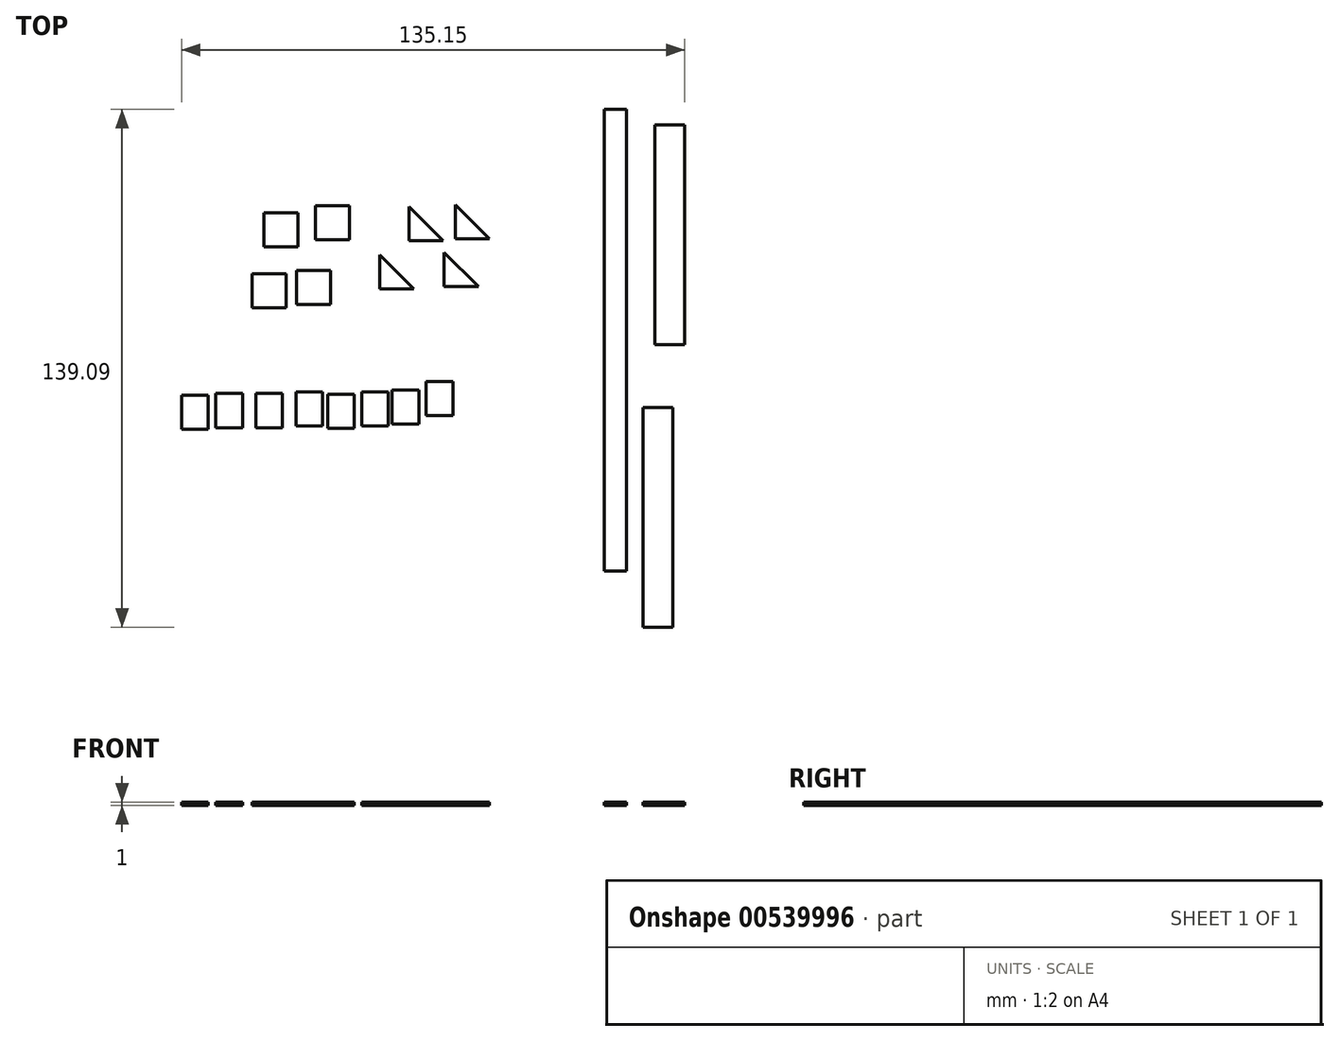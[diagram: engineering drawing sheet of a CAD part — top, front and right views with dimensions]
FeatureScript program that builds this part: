
annotation { "Feature Type Name" : "Feature", "Feature Type Description" : "" }
export const myFeature = defineFeature(function(context is Context, id is Id, definition is map)
    precondition{}
    {
        {
            var Q0;
            Q0=qCreatedBy(makeId("Top.planeOp"),FACE);
            var sketch = newSketch(context, id + "F0", { "sketchPlane" : qUnion([Q0])});
            skLineSegment(sketch, "E0.bottom", {"start": v(-71.16, 32.3) * mm, "end": v(-80.3, 32.3) * mm});
            skLineSegment(sketch, "E0.top", {"start": v(-71.16, 41.45) * mm, "end": v(-80.3, 41.45) * mm});
            skLineSegment(sketch, "E0.left", {"start": v(-71.16, 32.3) * mm, "end": v(-71.16, 41.45) * mm});
            skLineSegment(sketch, "E0.right", {"start": v(-80.3, 32.3) * mm, "end": v(-80.3, 41.45) * mm});
            skPoint(sketch, "E0.middle", {"position": v(-75.73, 36.88) * mm});
            skLineSegment(sketch, "E1.bottom", {"start": v(-74.39, 15.94) * mm, "end": v(-83.54, 15.94) * mm});
            skLineSegment(sketch, "E1.top", {"start": v(-74.39, 25.09) * mm, "end": v(-83.54, 25.09) * mm});
            skLineSegment(sketch, "E1.left", {"start": v(-74.39, 15.94) * mm, "end": v(-74.39, 25.09) * mm});
            skLineSegment(sketch, "E1.right", {"start": v(-83.54, 15.94) * mm, "end": v(-83.54, 25.09) * mm});
            skPoint(sketch, "E1.middle", {"position": v(-78.96, 20.51) * mm});
            skLineSegment(sketch, "E2.bottom", {"start": v(-57.33, 34.15) * mm, "end": v(-66.48, 34.15) * mm});
            skLineSegment(sketch, "E2.top", {"start": v(-57.33, 43.3) * mm, "end": v(-66.48, 43.3) * mm});
            skLineSegment(sketch, "E2.left", {"start": v(-57.33, 34.15) * mm, "end": v(-57.33, 43.3) * mm});
            skLineSegment(sketch, "E2.right", {"start": v(-66.48, 34.15) * mm, "end": v(-66.48, 43.3) * mm});
            skPoint(sketch, "E2.middle", {"position": v(-61.9, 38.72) * mm});
            skLineSegment(sketch, "E3.bottom", {"start": v(-62.4, 16.74) * mm, "end": v(-71.55, 16.74) * mm});
            skLineSegment(sketch, "E3.top", {"start": v(-62.4, 25.9) * mm, "end": v(-71.55, 25.9) * mm});
            skLineSegment(sketch, "E3.left", {"start": v(-62.4, 16.74) * mm, "end": v(-62.4, 25.9) * mm});
            skLineSegment(sketch, "E3.right", {"start": v(-71.55, 16.74) * mm, "end": v(-71.55, 25.9) * mm});
            skPoint(sketch, "E3.middle", {"position": v(-66.97, 21.32) * mm});
            skLineSegment(sketch, "E4", {"start": v(-41.27, 43.03) * mm, "end": v(-41.27, 33.88) * mm});
            skLineSegment(sketch, "E5", {"start": v(-41.27, 33.88) * mm, "end": v(-32.12, 33.88) * mm});
            skLineSegment(sketch, "E6", {"start": v(-41.27, 43.03) * mm, "end": v(-32.12, 33.88) * mm});
            skLineSegment(sketch, "E7", {"start": v(-49.16, 30.07) * mm, "end": v(-49.16, 20.92) * mm});
            skLineSegment(sketch, "E8", {"start": v(-49.16, 20.92) * mm, "end": v(-40.01, 20.92) * mm});
            skLineSegment(sketch, "E9", {"start": v(-49.16, 30.07) * mm, "end": v(-40.01, 20.92) * mm});
            skLineSegment(sketch, "E10", {"start": v(-31.87, 30.76) * mm, "end": v(-31.87, 21.61) * mm});
            skLineSegment(sketch, "E11", {"start": v(-31.87, 21.61) * mm, "end": v(-22.72, 21.61) * mm});
            skLineSegment(sketch, "E12", {"start": v(-31.87, 30.76) * mm, "end": v(-22.72, 21.61) * mm});
            skLineSegment(sketch, "E13", {"start": v(-28.87, 43.56) * mm, "end": v(-28.87, 34.4) * mm});
            skLineSegment(sketch, "E14", {"start": v(-28.87, 34.4) * mm, "end": v(-19.72, 34.4) * mm});
            skLineSegment(sketch, "E15", {"start": v(-28.87, 43.56) * mm, "end": v(-19.72, 34.4) * mm});
            skSolve(sketch);
        }
        {
            var Q0;
            Q0=makeQuery(id+"F0.imprint","IMPRINT",FACE,{"disambiguationData":[TD([[makeQuery(id+"F0.imprint","IMPRINT",EDGE,{"derivedFrom":sQuery(id+"F0.wireOp",EDGE,"E0.bottom")}),-1.0]])]});
            var Q1;
            Q1=makeQuery(id+"F0.imprint","IMPRINT",FACE,{"disambiguationData":[TD([[makeQuery(id+"F0.imprint","IMPRINT",EDGE,{"derivedFrom":sQuery(id+"F0.wireOp",EDGE,"E1.bottom")}),-1.0]])]});
            var Q2;
            Q2=makeQuery(id+"F0.imprint","IMPRINT",FACE,{"disambiguationData":[TD([[makeQuery(id+"F0.imprint","IMPRINT",EDGE,{"derivedFrom":sQuery(id+"F0.wireOp",EDGE,"E2.bottom")}),-1.0]])]});
            var Q3;
            Q3=makeQuery(id+"F0.imprint","IMPRINT",FACE,{"disambiguationData":[TD([[makeQuery(id+"F0.imprint","IMPRINT",EDGE,{"derivedFrom":sQuery(id+"F0.wireOp",EDGE,"E3.bottom")}),-1.0]])]});
            var Q4;
            Q4=makeQuery(id+"F0.imprint","IMPRINT",FACE,{"disambiguationData":[TD([[makeQuery(id+"F0.imprint","IMPRINT",EDGE,{"derivedFrom":sQuery(id+"F0.wireOp",EDGE,"E7")}),1.0]])]});
            var Q5;
            Q5=makeQuery(id+"F0.imprint","IMPRINT",FACE,{"disambiguationData":[TD([[makeQuery(id+"F0.imprint","IMPRINT",EDGE,{"derivedFrom":sQuery(id+"F0.wireOp",EDGE,"E10")}),1.0]])]});
            var Q6;
            Q6=makeQuery(id+"F0.imprint","IMPRINT",FACE,{"disambiguationData":[TD([[makeQuery(id+"F0.imprint","IMPRINT",EDGE,{"derivedFrom":sQuery(id+"F0.wireOp",EDGE,"E4")}),1.0]])]});
            var Q7;
            Q7=makeQuery(id+"F0.imprint","IMPRINT",FACE,{"disambiguationData":[TD([[makeQuery(id+"F0.imprint","IMPRINT",EDGE,{"derivedFrom":sQuery(id+"F0.wireOp",EDGE,"E13")}),1.0]])]});
            extrude(context, id + "F1", {"entities" : qUnion([Q0, Q1, Q2, Q3, Q4, Q5, Q6, Q7]), "depth" : 1 * mm, "offsetDistance" : 25 * mm});
        }
        {
            var Q0;
            Q0=qCreatedBy(makeId("Top.planeOp"),FACE);
            var sketch = newSketch(context, id + "F2", { "sketchPlane" : qUnion([Q0])});
            skLineSegment(sketch, "E16.bottom", {"start": v(-95.29, -16.75) * mm, "end": v(-102.44, -16.75) * mm});
            skLineSegment(sketch, "E16.top", {"start": v(-95.29, -7.6) * mm, "end": v(-102.44, -7.6) * mm});
            skLineSegment(sketch, "E16.left", {"start": v(-95.29, -16.75) * mm, "end": v(-95.29, -7.6) * mm});
            skLineSegment(sketch, "E16.right", {"start": v(-102.44, -16.75) * mm, "end": v(-102.44, -7.6) * mm});
            skPoint(sketch, "E16.middle", {"position": v(-98.86, -12.18) * mm});
            skLineSegment(sketch, "E17.bottom", {"start": v(-86.08, -16.3) * mm, "end": v(-93.23, -16.3) * mm});
            skLineSegment(sketch, "E17.top", {"start": v(-86.08, -7.15) * mm, "end": v(-93.23, -7.15) * mm});
            skLineSegment(sketch, "E17.left", {"start": v(-86.08, -16.3) * mm, "end": v(-86.08, -7.15) * mm});
            skLineSegment(sketch, "E17.right", {"start": v(-93.23, -16.3) * mm, "end": v(-93.23, -7.15) * mm});
            skPoint(sketch, "E17.middle", {"position": v(-89.65, -11.73) * mm});
            skLineSegment(sketch, "E18.bottom", {"start": v(-75.3, -16.3) * mm, "end": v(-82.45, -16.3) * mm});
            skLineSegment(sketch, "E18.top", {"start": v(-75.3, -7.15) * mm, "end": v(-82.45, -7.15) * mm});
            skLineSegment(sketch, "E18.left", {"start": v(-75.3, -16.3) * mm, "end": v(-75.3, -7.15) * mm});
            skLineSegment(sketch, "E18.right", {"start": v(-82.45, -16.3) * mm, "end": v(-82.45, -7.15) * mm});
            skPoint(sketch, "E18.middle", {"position": v(-78.87, -11.73) * mm});
            skLineSegment(sketch, "E19.bottom", {"start": v(-64.52, -15.81) * mm, "end": v(-71.67, -15.81) * mm});
            skLineSegment(sketch, "E19.top", {"start": v(-64.52, -6.66) * mm, "end": v(-71.67, -6.66) * mm});
            skLineSegment(sketch, "E19.left", {"start": v(-64.52, -15.81) * mm, "end": v(-64.52, -6.66) * mm});
            skLineSegment(sketch, "E19.right", {"start": v(-71.67, -15.81) * mm, "end": v(-71.67, -6.66) * mm});
            skPoint(sketch, "E19.middle", {"position": v(-68.1, -11.24) * mm});
            skLineSegment(sketch, "E20.bottom", {"start": v(-56.02, -16.47) * mm, "end": v(-63.17, -16.47) * mm});
            skLineSegment(sketch, "E20.top", {"start": v(-56.02, -7.32) * mm, "end": v(-63.17, -7.32) * mm});
            skLineSegment(sketch, "E20.left", {"start": v(-56.02, -16.47) * mm, "end": v(-56.02, -7.32) * mm});
            skLineSegment(sketch, "E20.right", {"start": v(-63.17, -16.47) * mm, "end": v(-63.17, -7.32) * mm});
            skPoint(sketch, "E20.middle", {"position": v(-59.6, -11.9) * mm});
            skLineSegment(sketch, "E21.bottom", {"start": v(-46.88, -15.81) * mm, "end": v(-54.03, -15.81) * mm});
            skLineSegment(sketch, "E21.top", {"start": v(-46.88, -6.66) * mm, "end": v(-54.03, -6.66) * mm});
            skLineSegment(sketch, "E21.left", {"start": v(-46.88, -15.81) * mm, "end": v(-46.88, -6.66) * mm});
            skLineSegment(sketch, "E21.right", {"start": v(-54.03, -15.81) * mm, "end": v(-54.03, -6.66) * mm});
            skPoint(sketch, "E21.middle", {"position": v(-50.45, -11.24) * mm});
            skLineSegment(sketch, "E22.bottom", {"start": v(-38.71, -15.32) * mm, "end": v(-45.86, -15.32) * mm});
            skLineSegment(sketch, "E22.top", {"start": v(-38.71, -6.17) * mm, "end": v(-45.86, -6.17) * mm});
            skLineSegment(sketch, "E22.left", {"start": v(-38.71, -15.32) * mm, "end": v(-38.71, -6.17) * mm});
            skLineSegment(sketch, "E22.right", {"start": v(-45.86, -15.32) * mm, "end": v(-45.86, -6.17) * mm});
            skPoint(sketch, "E22.middle", {"position": v(-42.29, -10.75) * mm});
            skLineSegment(sketch, "E23.bottom", {"start": v(-29.57, -13.04) * mm, "end": v(-36.72, -13.04) * mm});
            skLineSegment(sketch, "E23.top", {"start": v(-29.57, -3.89) * mm, "end": v(-36.72, -3.89) * mm});
            skLineSegment(sketch, "E23.left", {"start": v(-29.57, -13.04) * mm, "end": v(-29.57, -3.89) * mm});
            skLineSegment(sketch, "E23.right", {"start": v(-36.72, -13.04) * mm, "end": v(-36.72, -3.89) * mm});
            skPoint(sketch, "E23.middle", {"position": v(-33.14, -8.46) * mm});
            skSolve(sketch);
        }
        {
            var Q0;
            Q0 = qSketchRegion(id + "F2", true);
            extrude(context, id + "F3", {"entities" : qUnion([Q0]), "depth" : 1 * mm, "offsetDistance" : 25 * mm});
        }
        {
            var Q0;
            Q0=qCreatedBy(makeId("Top.planeOp"),FACE);
            var sketch = newSketch(context, id + "F4", { "sketchPlane" : qUnion([Q0])});
            skLineSegment(sketch, "E24.bottom", {"start": v(11.14, 69.19) * mm, "end": v(17.14, 69.19) * mm});
            skLineSegment(sketch, "E24.top", {"start": v(11.14, -54.86) * mm, "end": v(17.14, -54.86) * mm});
            skLineSegment(sketch, "E24.left", {"start": v(11.14, 69.19) * mm, "end": v(11.14, -54.86) * mm});
            skLineSegment(sketch, "E24.right", {"start": v(17.14, 69.19) * mm, "end": v(17.14, -54.86) * mm});
            skLineSegment(sketch, "E25.bottom", {"start": v(24.69, 65.02) * mm, "end": v(32.71, 65.02) * mm});
            skLineSegment(sketch, "E25.top", {"start": v(24.69, 6) * mm, "end": v(32.71, 6) * mm});
            skLineSegment(sketch, "E25.left", {"start": v(24.69, 65.02) * mm, "end": v(24.69, 6) * mm});
            skLineSegment(sketch, "E25.right", {"start": v(32.71, 65.02) * mm, "end": v(32.71, 6) * mm});
            skLineSegment(sketch, "E26.bottom", {"start": v(21.54, -10.87) * mm, "end": v(29.56, -10.87) * mm});
            skLineSegment(sketch, "E26.top", {"start": v(21.54, -69.9) * mm, "end": v(29.56, -69.9) * mm});
            skLineSegment(sketch, "E26.left", {"start": v(21.54, -10.87) * mm, "end": v(21.54, -69.9) * mm});
            skLineSegment(sketch, "E26.right", {"start": v(29.56, -10.87) * mm, "end": v(29.56, -69.9) * mm});
            skSolve(sketch);
        }
        {
            var Q0;
            Q0=makeQuery(id+"F4.imprint","IMPRINT",FACE,{"disambiguationData":[TD([[makeQuery(id+"F4.imprint","IMPRINT",EDGE,{"derivedFrom":sQuery(id+"F4.wireOp",EDGE,"E24.bottom")}),-1.0]])]});
            var Q1;
            Q1=makeQuery(id+"F4.imprint","IMPRINT",FACE,{"disambiguationData":[TD([[makeQuery(id+"F4.imprint","IMPRINT",EDGE,{"derivedFrom":sQuery(id+"F4.wireOp",EDGE,"E25.bottom")}),-1.0]])]});
            var Q2;
            Q2=makeQuery(id+"F4.imprint","IMPRINT",FACE,{"disambiguationData":[TD([[makeQuery(id+"F4.imprint","IMPRINT",EDGE,{"derivedFrom":sQuery(id+"F4.wireOp",EDGE,"E26.bottom")}),-1.0]])]});
            extrude(context, id + "F5", {"entities" : qUnion([Q0, Q1, Q2]), "depth" : 1 * mm, "offsetDistance" : 25 * mm});
        }
    });
